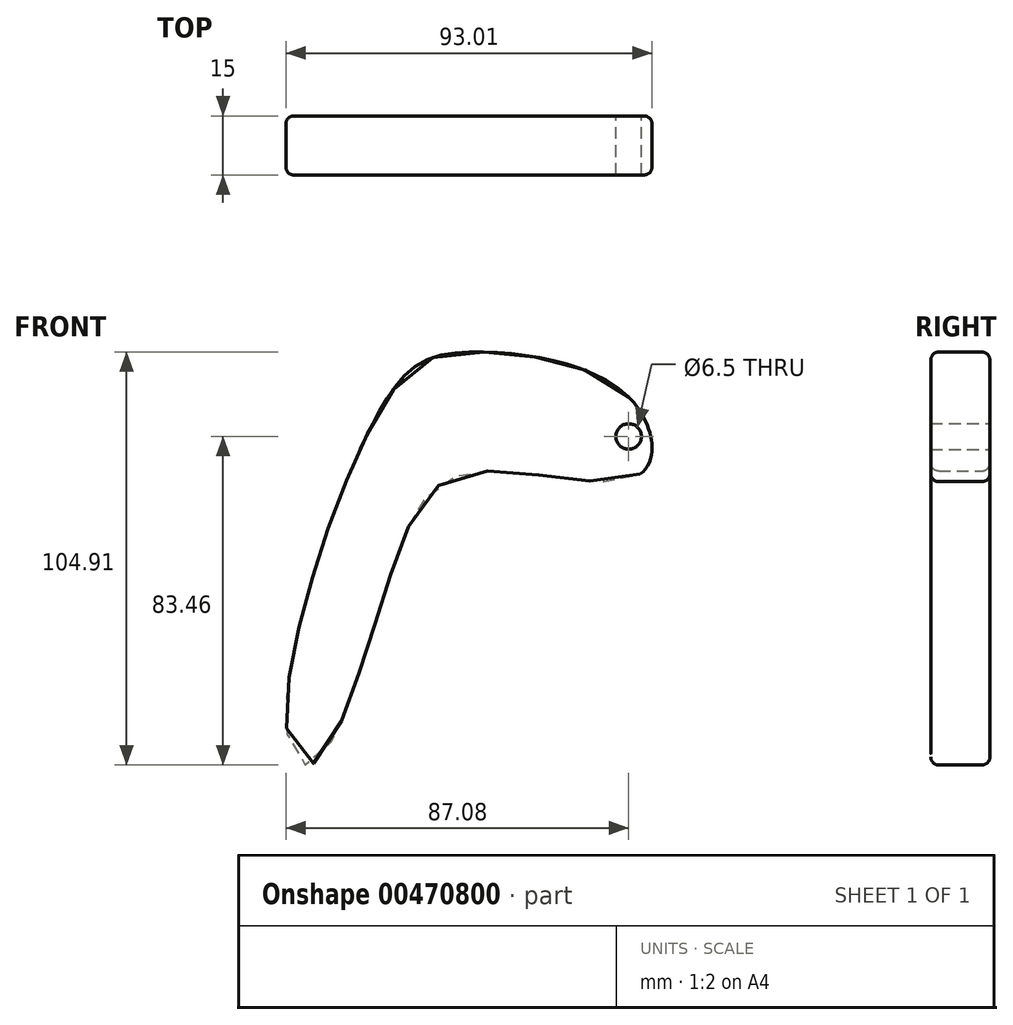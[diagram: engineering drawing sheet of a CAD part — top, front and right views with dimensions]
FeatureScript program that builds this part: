
annotation { "Feature Type Name" : "Feature", "Feature Type Description" : "" }
export const myFeature = defineFeature(function(context is Context, id is Id, definition is map)
    precondition{}
    {
        {
            var Q0;
            Q0=qCreatedBy(makeId("Front.planeOp"),FACE);
            var sketch = newSketch(context, id + "F0", { "sketchPlane" : qUnion([Q0])});
            skCircle(sketch, "E0", {"center": v(0, 0) * mm, "radius": 3.25 * mm});
            skCircle(sketch, "E1", {"center": v(0, 0) * mm, "radius": 10 * mm});
            skFitSpline(sketch, "E2", {"points": [v(0, 10) * mm, v(-41.33, 21.39) * mm, v(-61.63, 9.24) * mm, v(-86.8, -75.54) * mm, v(-79.94, -83) * mm, v(-59.63, -32.52) * mm, v(-39.61, -9) * mm, v(2.88, -9.58) * mm, v(0, 10) * mm]});
            skSolve(sketch);
        }
        {
            var Q0;
            {var subQ0=sQuery(id+"F0.wireOp",EDGE,"E2");var subQ1=sQuery(id+"F0.wireOp",EDGE,"E1");var subQ2=makeQuery(id+"F0.imprint","INTERSECT",VERTEX,{"disambiguationData":[OD(0.0)],"derivedFrom":[subQ1,subQ0]});Q0=makeQuery(id+"F0.imprint","IMPRINT",FACE,{"disambiguationData":[TD([[makeQuery(id+"F0.imprint","IMPRINT",EDGE,{"disambiguationData":[TD([[subQ2,1.0]])],"derivedFrom":subQ1}),-1.0]])]});}
            var Q1;
            Q1=makeQuery(id+"F0.imprint","IMPRINT",FACE,{"disambiguationData":[TD([[makeQuery(id+"F0.imprint","IMPRINT",EDGE,{"derivedFrom":sQuery(id+"F0.wireOp",EDGE,"E0")}),-1.0]])]});
            extrude(context, id + "F1", {"entities" : qUnion([Q0, Q1]), "endBound" : BoundingType.SYMMETRIC, "depth" : 15 * mm});
        }
        {
            var Q0;
            Q0=makeQuery(id+"F1.opExtrude","CAP_EDGE",EDGE,{"disambiguationData":[OSD([sQuery(id+"F0.wireOp",EDGE,"E2")])],"isStart":false});
            var Q1;
            Q1=makeQuery(id+"F1.opExtrude","CAP_EDGE",EDGE,{"disambiguationData":[OSD([sQuery(id+"F0.wireOp",EDGE,"E2")])],"isStart":true});
            fillet(context, id + "F2", {"entities" : qUnion([Q0, Q1]), "radius" : 2 * mm, "tangentPropagation" : true, "allowEdgeOverflow" : false});
        }
    });
